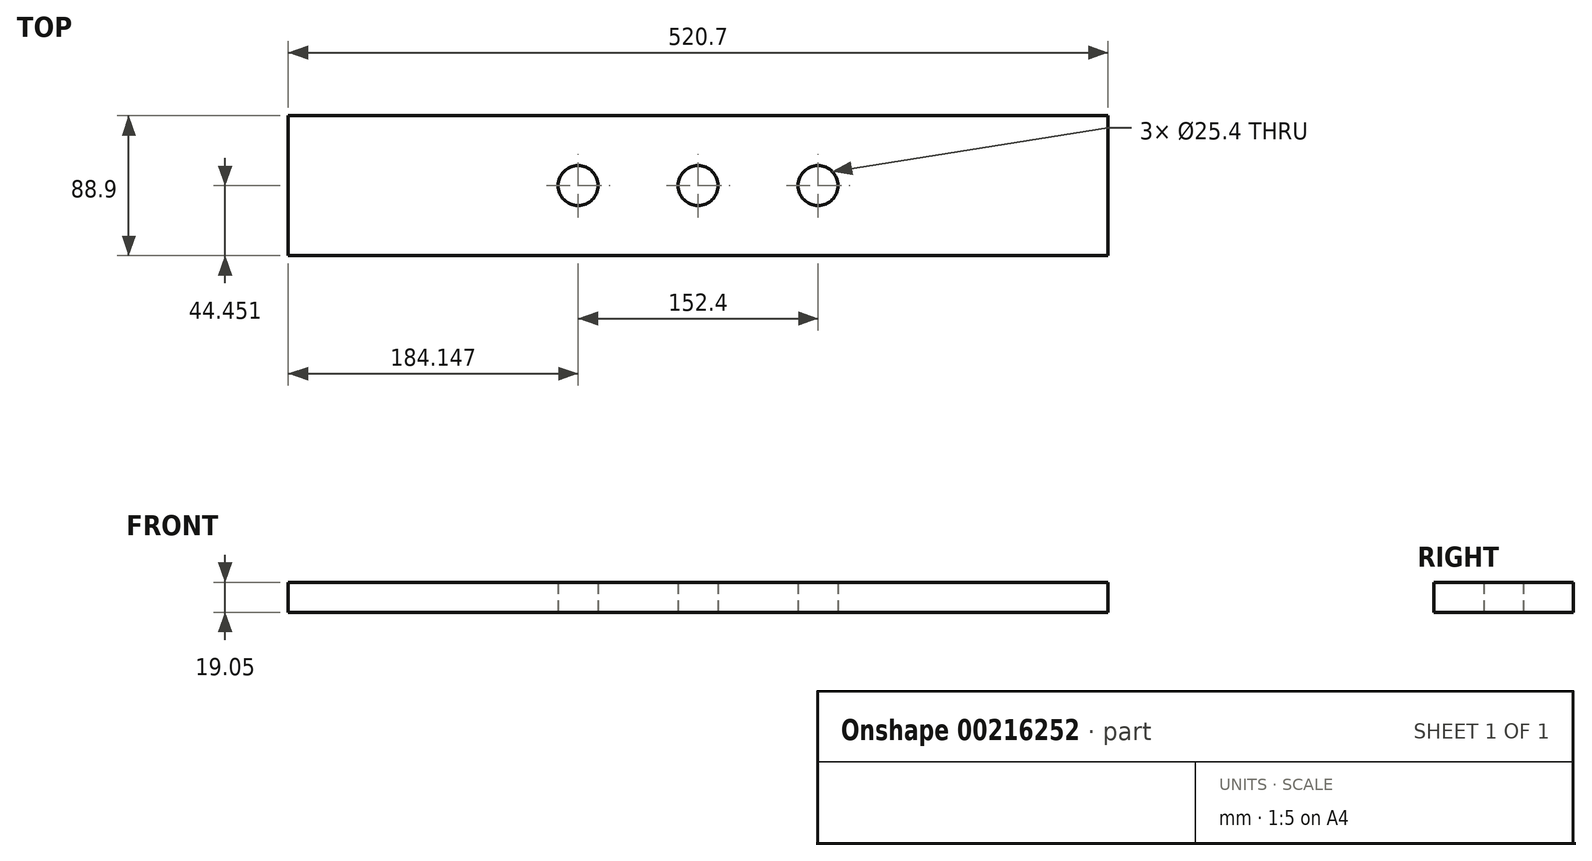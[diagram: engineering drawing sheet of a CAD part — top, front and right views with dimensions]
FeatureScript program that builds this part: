
annotation { "Feature Type Name" : "Feature", "Feature Type Description" : "" }
export const myFeature = defineFeature(function(context is Context, id is Id, definition is map)
    precondition{}
    {
        {
            var Q0;
            Q0=qCreatedBy(makeId("Top.planeOp"),FACE);
            var sketch = newSketch(context, id + "F0", { "sketchPlane" : qUnion([Q0])});
            skLineSegment(sketch, "E0", {"start": v(-4579.92, -2621.24) * mm, "end": v(-4059.22, -2621.24) * mm});
            skLineSegment(sketch, "E1", {"start": v(-4059.22, -2621.24) * mm, "end": v(-4059.22, -2532.34) * mm});
            skLineSegment(sketch, "E2", {"start": v(-4059.22, -2532.34) * mm, "end": v(-4579.92, -2532.34) * mm});
            skLineSegment(sketch, "E3", {"start": v(-4579.92, -2532.34) * mm, "end": v(-4579.92, -2621.24) * mm});
            skCircle(sketch, "E4", {"center": v(-4319.57, -2576.79) * mm, "radius": 12.7 * mm});
            skCircle(sketch, "E5", {"center": v(-4243.37, -2576.79) * mm, "radius": 12.7 * mm});
            skCircle(sketch, "E6", {"center": v(-4395.77, -2576.79) * mm, "radius": 12.7 * mm});
            skSolve(sketch);
        }
        {
            var Q0;
            Q0=makeQuery(id+"F0.imprint","IMPRINT",FACE,{"disambiguationData":[TD([[makeQuery(id+"F0.imprint","IMPRINT",EDGE,{"derivedFrom":sQuery(id+"F0.wireOp",EDGE,"E0")}),1.0]])]});
            extrude(context, id + "F1", {"entities" : qUnion([Q0]), "depth" : 19.05 * mm});
        }
    });
